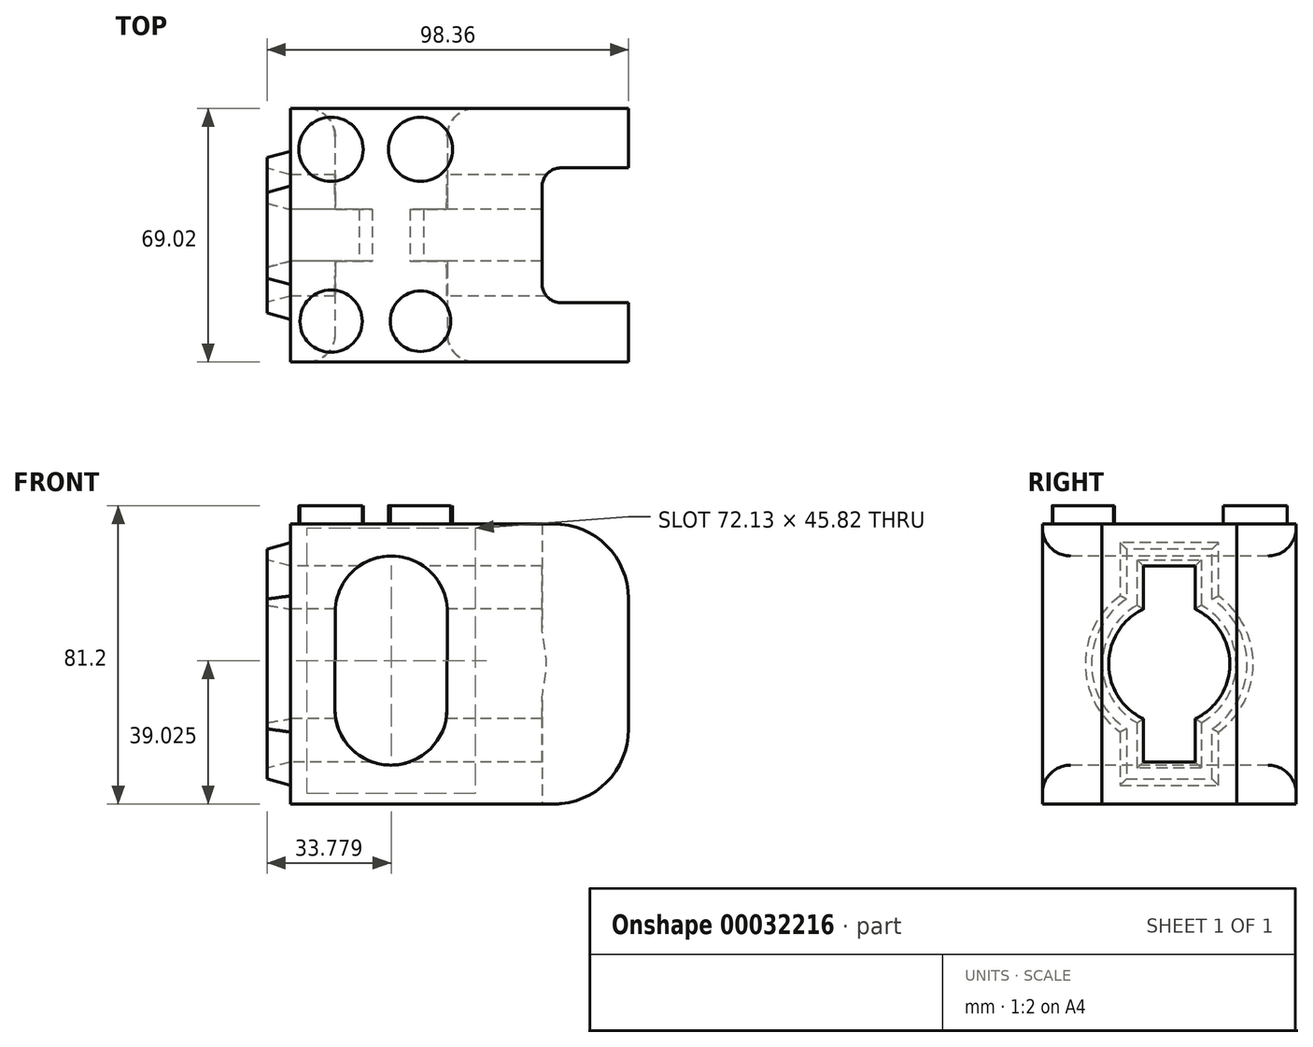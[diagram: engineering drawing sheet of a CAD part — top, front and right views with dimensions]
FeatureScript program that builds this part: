
annotation { "Feature Type Name" : "Feature", "Feature Type Description" : "" }
export const myFeature = defineFeature(function(context is Context, id is Id, definition is map)
    precondition{}
    {
        {
            var Q0;
            Q0=qCreatedBy(makeId("Top.planeOp"),FACE);
            var sketch = newSketch(context, id + "F0", { "sketchPlane" : qUnion([Q0])});
            skLineSegment(sketch, "E0", {"start": v(-54.6, 34.5) * mm, "end": v(37.41, 34.5) * mm});
            skLineSegment(sketch, "E1", {"start": v(37.41, 34.5) * mm, "end": v(37.41, 18.33) * mm});
            skLineSegment(sketch, "E2", {"start": v(37.41, 18.33) * mm, "end": v(13.9, 18.33) * mm});
            skLineSegment(sketch, "E3", {"start": v(13.9, 18.33) * mm, "end": v(13.9, 0) * mm});
            skLineSegment(sketch, "E4", {"start": v(13.9, 0) * mm, "end": v(-54.6, 0) * mm});
            skLineSegment(sketch, "E5", {"start": v(-54.6, 0) * mm, "end": v(-54.6, 34.5) * mm});
            skLineSegment(sketch, "E6", {"start": v(-76.1, 0) * mm, "end": v(70.28, 0) * mm, "construction": true});
            skLineSegment(sketch, "E7.MirrorCS", {"start": v(-54.6, -34.5) * mm, "end": v(37.41, -34.5) * mm});
            skLineSegment(sketch, "E8.MirrorCS", {"start": v(-54.6, 0) * mm, "end": v(-54.6, -34.5) * mm});
            skLineSegment(sketch, "E9.MirrorCS", {"start": v(13.9, -18.33) * mm, "end": v(13.9, 0) * mm});
            skLineSegment(sketch, "E10.MirrorCS", {"start": v(37.41, -18.33) * mm, "end": v(13.9, -18.33) * mm});
            skLineSegment(sketch, "E11.MirrorCS", {"start": v(37.41, -34.5) * mm, "end": v(37.41, -18.33) * mm});
            skSolve(sketch);
        }
        {
            var Q0;
            Q0=makeQuery(id+"F0.imprint","IMPRINT",FACE,{"disambiguationData":[TD([[makeQuery(id+"F0.imprint","IMPRINT",EDGE,{"derivedFrom":sQuery(id+"F0.wireOp",EDGE,"E4")}),1.0]])]});
            var Q1;
            Q1=makeQuery(id+"F0.imprint","IMPRINT",FACE,{"disambiguationData":[TD([[makeQuery(id+"F0.imprint","IMPRINT",EDGE,{"derivedFrom":sQuery(id+"F0.wireOp",EDGE,"E0")}),-1.0]])]});
            extrude(context, id + "F1", {"entities" : qUnion([Q0, Q1]), "depth" : 76.2 * mm});
        }
        {
            var Q0;
            Q0=makeQuery(id+"F1.opExtrude","CAP_EDGE",EDGE,{"disambiguationData":[OSD([sQuery(id+"F0.wireOp",EDGE,"E11.MirrorCS")])],"isStart":false});
            var Q1;
            Q1=makeQuery(id+"F1.opExtrude","CAP_EDGE",EDGE,{"disambiguationData":[OSD([sQuery(id+"F0.wireOp",EDGE,"E1")])],"isStart":false});
            var Q2;
            Q2=makeQuery(id+"F1.opExtrude","CAP_EDGE",EDGE,{"disambiguationData":[OSD([sQuery(id+"F0.wireOp",EDGE,"E1")])],"isStart":true});
            var Q3;
            Q3=makeQuery(id+"F1.opExtrude","CAP_EDGE",EDGE,{"disambiguationData":[OSD([sQuery(id+"F0.wireOp",EDGE,"E11.MirrorCS")])],"isStart":true});
            fillet(context, id + "F2", {"entities" : qUnion([Q0, Q1, Q2, Q3]), "radius" : 20.32 * mm, "allowEdgeOverflow" : false});
        }
        {
            var Q0;
            Q0=makeQuery(id+"F1.opExtrude","SWEPT_EDGE",EDGE,{"disambiguationData":[OSD([sQuery(id+"F0.wireOp",EDGE,"E2"),sQuery(id+"F0.wireOp",EDGE,"E3")])]});
            var Q1;
            Q1=makeQuery(id+"F1.opExtrude","SWEPT_EDGE",EDGE,{"disambiguationData":[OSD([sQuery(id+"F0.wireOp",EDGE,"E9.MirrorCS"),sQuery(id+"F0.wireOp",EDGE,"E10.MirrorCS")])]});
            fillet(context, id + "F3", {"entities" : qUnion([Q0, Q1]), "radius" : 5.08 * mm, "tangentPropagation" : true, "allowEdgeOverflow" : false});
        }
        {
            var Q0;
            Q0=makeQuery(id+"F1.opExtrude","SWEPT_FACE",FACE,{"disambiguationData":[OSD([sQuery(id+"F0.wireOp",EDGE,"E7.MirrorCS")])]});
            var sketch = newSketch(context, id + "F4", { "sketchPlane" : qUnion([Q0])});
            skLineSegment(sketch, "E12.left", {"start": v(-42.46, 25.88) * mm, "end": v(-42.36, 52.3) * mm});
            skLineSegment(sketch, "E12.right", {"start": v(-11.98, 25.76) * mm, "end": v(-11.88, 52.17) * mm});
            skArc(sketch, "E13", {"start": v(-11.88, 52.17) * mm, "mid": v(-27.06, 67.47) * mm, "end": v(-42.36, 52.3) * mm});
            skArc(sketch, "E14", {"start": v(-42.46, 25.88) * mm, "mid": v(-27.28, 10.58) * mm, "end": v(-11.98, 25.76) * mm});
            skSolve(sketch);
        }
        {
            var Q0;
            Q0=makeQuery(id+"F4.imprint","IMPRINT",FACE,{"disambiguationData":[TD([[makeQuery(id+"F4.imprint","IMPRINT",EDGE,{"derivedFrom":sQuery(id+"F4.wireOp",EDGE,"E12.left")}),-1.0]])]});
            extrude(context, id + "F5", {"entities" : qUnion([Q0]), "operationType" : NewBodyOperationType.REMOVE, "endBound" : BoundingType.THROUGH_ALL, "oppositeDirection" : true, "depth" : 25.4 * mm});
        }
        {
            var Q0;
            Q0=makeQuery(id+"F5.boolean.opBoolean","COPY",FACE,{"derivedFrom":makeQuery(id+"F5.opExtrude","SWEPT_FACE",FACE,{"disambiguationData":[OSD([sQuery(id+"F4.wireOp",EDGE,"E13")])]})});
            fillet(context, id + "F6", {"entities" : qUnion([Q0]), "radius" : 7.62 * mm, "tangentPropagation" : true, "allowEdgeOverflow" : false});
        }
        {
            var Q0;
            Q0=makeQuery(id+"F1.opExtrude","SWEPT_FACE",FACE,{"disambiguationData":[OSD([sQuery(id+"F0.wireOp",EDGE,"E5"),sQuery(id+"F0.wireOp",EDGE,"E8.MirrorCS")])]});
            var sketch = newSketch(context, id + "F7", { "sketchPlane" : qUnion([Q0])});
            skArc(sketch, "E15", {"start": v(7.02, 23.17) * mm, "mid": v(16.5, 38.1) * mm, "end": v(7.02, 53.03) * mm});
            skPoint(sketch, "E15.centerSnap0", {"position": v(-34.5, 38.1) * mm});
            skLineSegment(sketch, "E16.rect.bottom", {"start": v(7.02, 11.47) * mm, "end": v(-7.02, 11.47) * mm});
            skLineSegment(sketch, "E16.rect.top", {"start": v(7.02, 64.73) * mm, "end": v(-7.02, 64.73) * mm});
            skLineSegment(sketch, "E16.rect.left", {"start": v(7.02, 11.47) * mm, "end": v(7.02, 23.17) * mm});
            skLineSegment(sketch, "E16.rect.right", {"start": v(-7.02, 11.47) * mm, "end": v(-7.02, 23.17) * mm});
            skLineSegment(sketch, "E17.trimOffspring", {"start": v(7.02, 53.03) * mm, "end": v(7.02, 64.73) * mm});
            skLineSegment(sketch, "E18.trimOffspring", {"start": v(-7.02, 53.03) * mm, "end": v(-7.02, 64.73) * mm});
            skArc(sketch, "E19.trimOffspring", {"start": v(-7.02, 53.03) * mm, "mid": v(-16.5, 38.1) * mm, "end": v(-7.02, 23.17) * mm});
            skLineSegment(sketch, "E20.0", {"start": v(-13.37, 56.62) * mm, "end": v(-13.37, 71.08) * mm});
            skLineSegment(sketch, "E20.1", {"start": v(13.37, 71.08) * mm, "end": v(-13.37, 71.08) * mm});
            skLineSegment(sketch, "E20.2", {"start": v(13.37, 56.62) * mm, "end": v(13.37, 71.08) * mm});
            skArc(sketch, "E20.3", {"start": v(13.37, 19.58) * mm, "mid": v(22.84, 38.1) * mm, "end": v(13.37, 56.62) * mm});
            skLineSegment(sketch, "E20.4", {"start": v(13.37, 5.12) * mm, "end": v(13.37, 19.58) * mm});
            skArc(sketch, "E20.5", {"start": v(-13.37, 56.62) * mm, "mid": v(-22.84, 38.1) * mm, "end": v(-13.37, 19.58) * mm});
            skLineSegment(sketch, "E20.6", {"start": v(13.37, 5.12) * mm, "end": v(-13.37, 5.12) * mm});
            skLineSegment(sketch, "E20.7", {"start": v(-13.37, 5.12) * mm, "end": v(-13.37, 19.58) * mm});
            skSolve(sketch);
        }
        {
            var Q0;
            Q0=makeQuery(id+"F7.imprint","IMPRINT",FACE,{"disambiguationData":[TD([[makeQuery(id+"F7.imprint","IMPRINT",EDGE,{"derivedFrom":sQuery(id+"F7.wireOp",EDGE,"E15")}),1.0]])]});
            extrude(context, id + "F8", {"entities" : qUnion([Q0]), "operationType" : NewBodyOperationType.REMOVE, "endBound" : BoundingType.THROUGH_ALL, "oppositeDirection" : true, "depth" : 25.4 * mm});
        }
        {
            var Q0;
            Q0=makeQuery(id+"F7.imprint","IMPRINT",FACE,{"disambiguationData":[TD([[makeQuery(id+"F7.imprint","IMPRINT",EDGE,{"derivedFrom":sQuery(id+"F7.wireOp",EDGE,"E15")}),-1.0]])]});
            extrude(context, id + "F9", {"entities" : qUnion([Q0]), "operationType" : NewBodyOperationType.ADD, "depth" : 6.35 * mm, "hasDraft" : true, "draftAngle" : 15 * degree, "draftPullDirection" : true});
        }
        {
            var Q0;
            Q0=makeQuery(id+"F1.opExtrude","CAP_FACE",FACE,{"disambiguationData":[OSD([sQuery(id+"F0.wireOp",EDGE,"E0"),sQuery(id+"F0.wireOp",EDGE,"E1"),sQuery(id+"F0.wireOp",EDGE,"E2"),sQuery(id+"F0.wireOp",EDGE,"E3"),sQuery(id+"F0.wireOp",EDGE,"E5"),sQuery(id+"F0.wireOp",EDGE,"E7.MirrorCS"),sQuery(id+"F0.wireOp",EDGE,"E8.MirrorCS"),sQuery(id+"F0.wireOp",EDGE,"E9.MirrorCS"),sQuery(id+"F0.wireOp",EDGE,"E10.MirrorCS"),sQuery(id+"F0.wireOp",EDGE,"E11.MirrorCS")])],"isStart":false});
            var sketch = newSketch(context, id + "F10", { "sketchPlane" : qUnion([Q0])});
            skCircle(sketch, "E21", {"center": v(-43.51, 23.38) * mm, "radius": 8.74 * mm});
            skCircle(sketch, "E22", {"center": v(-19.18, 23.38) * mm, "radius": 8.75 * mm});
            skCircle(sketch, "E23", {"center": v(-43.51, -23.38) * mm, "radius": 8.47 * mm});
            skCircle(sketch, "E24", {"center": v(-19.18, -23.38) * mm, "radius": 8.24 * mm});
            skSolve(sketch);
        }
        {
            var Q0;
            Q0 = qSketchRegion(id + "F10", true);
            extrude(context, id + "F11", {"entities" : qUnion([Q0]), "operationType" : NewBodyOperationType.ADD, "depth" : 5 * mm});
        }
    });
